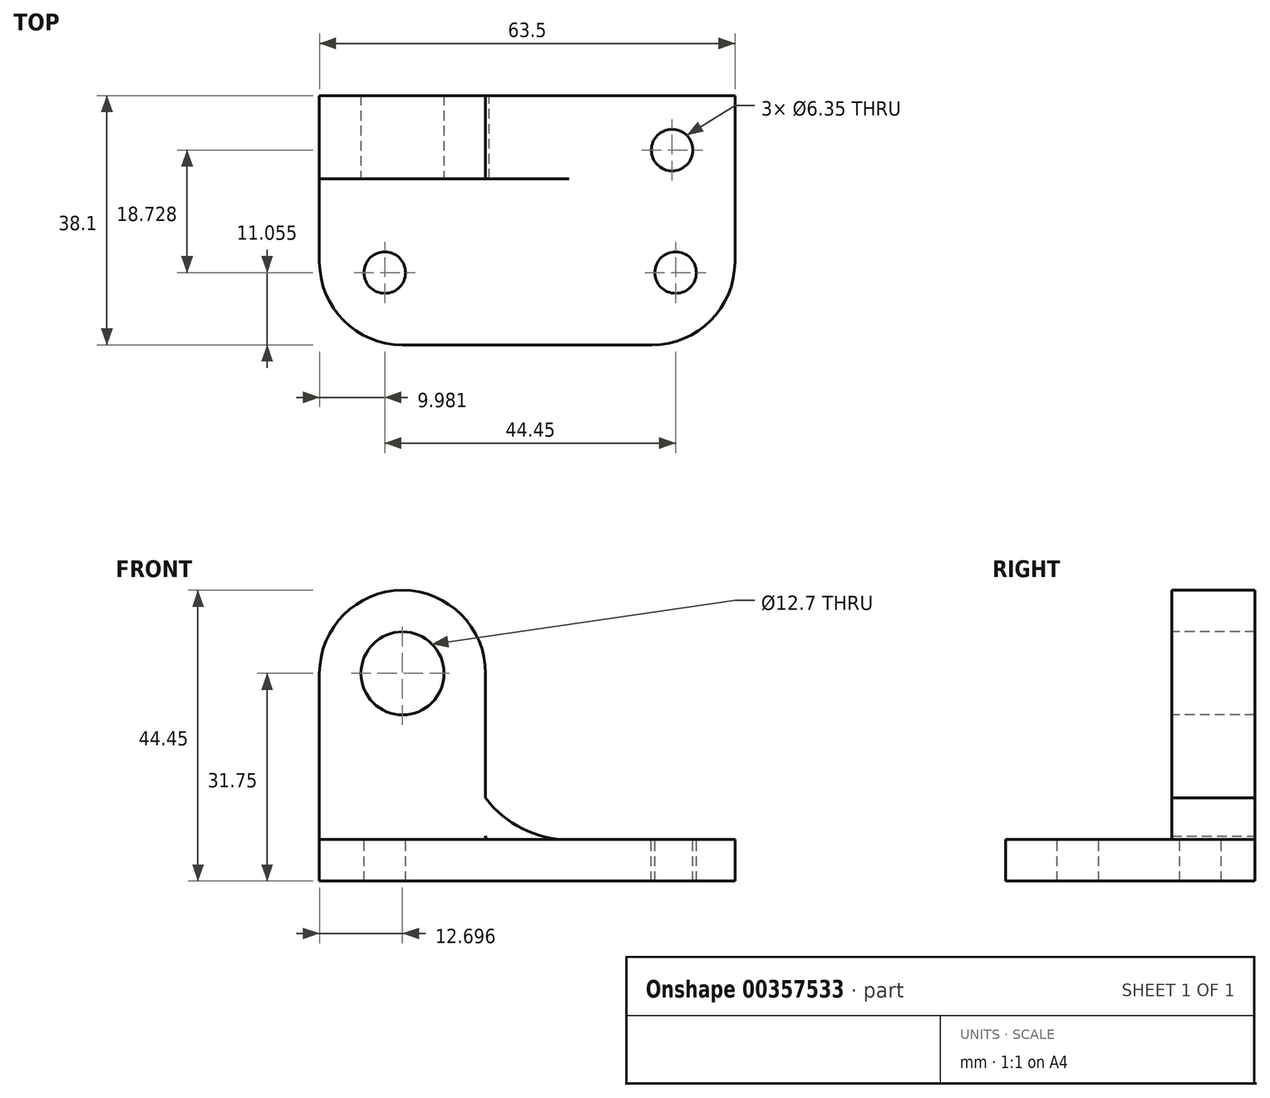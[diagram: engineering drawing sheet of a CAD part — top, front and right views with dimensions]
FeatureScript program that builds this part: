
annotation { "Feature Type Name" : "Feature", "Feature Type Description" : "" }
export const myFeature = defineFeature(function(context is Context, id is Id, definition is map)
    precondition{}
    {
        {
            var Q0;
            Q0=qCreatedBy(makeId("Front.planeOp"),FACE);
            var sketch = newSketch(context, id + "F0", { "sketchPlane" : qUnion([Q0])});
            skLineSegment(sketch, "E0", {"start": v(-62.41, 45.13) * mm, "end": v(-37.01, 45.13) * mm});
            skLineSegment(sketch, "E1", {"start": v(-37.01, 45.13) * mm, "end": v(-37.01, 7.03) * mm});
            skLineSegment(sketch, "E2", {"start": v(-37.01, 7.03) * mm, "end": v(1.09, 7.03) * mm});
            skLineSegment(sketch, "E3", {"start": v(1.09, 7.03) * mm, "end": v(1.09, 0.68) * mm});
            skLineSegment(sketch, "E4", {"start": v(1.09, 0.68) * mm, "end": v(-62.41, 0.68) * mm});
            skLineSegment(sketch, "E5", {"start": v(-62.41, 0.68) * mm, "end": v(-62.41, 45.13) * mm});
            skSolve(sketch);
        }
        {
            var Q0;
            Q0=makeQuery(id+"F0.imprint","IMPRINT",FACE,{"disambiguationData":[TD([[makeQuery(id+"F0.imprint","IMPRINT",EDGE,{"derivedFrom":sQuery(id+"F0.wireOp",EDGE,"E0")}),-1.0]])]});
            extrude(context, id + "F1", {"entities" : qUnion([Q0]), "depth" : 38.1 * mm});
        }
        {
            var Q0;
            Q0=makeQuery(id+"F1.opExtrude","CAP_FACE",FACE,{"disambiguationData":[OSD([sQuery(id+"F0.wireOp",EDGE,"E0"),sQuery(id+"F0.wireOp",EDGE,"E1"),sQuery(id+"F0.wireOp",EDGE,"E2"),sQuery(id+"F0.wireOp",EDGE,"E3"),sQuery(id+"F0.wireOp",EDGE,"E4"),sQuery(id+"F0.wireOp",EDGE,"E5")])],"isStart":false});
            var sketch = newSketch(context, id + "F2", { "sketchPlane" : qUnion([Q0])});
            skLineSegment(sketch, "E6", {"start": v(-37.01, 7.03) * mm, "end": v(-62.41, 7.03) * mm});
            skSolve(sketch);
        }
        {
            var Q0;
            {var subQ0=sQuery(id+"F2.wireOp",EDGE,"E6");Q0=makeQuery(id+"F2.imprint","IMPRINT",FACE,{"disambiguationData":[TD([[makeQuery(id+"F2.imprint","IMPRINT",EDGE,{"derivedFrom":subQ0}),-1.0]])]});}
            extrude(context, id + "F3", {"entities" : qUnion([Q0]), "operationType" : NewBodyOperationType.REMOVE, "oppositeDirection" : true, "depth" : 25.4 * mm});
        }
        {
            var Q0;
            Q0=makeQuery(id+"F3.boolean.opBoolean","COPY",FACE,{"derivedFrom":makeQuery(id+"F3.opExtrude","CAP_FACE",FACE,{"disambiguationData":[OSD([sQuery(id+"F0.wireOp",EDGE,"E0"),sQuery(id+"F0.wireOp",EDGE,"E1"),sQuery(id+"F0.wireOp",EDGE,"E5"),sQuery(id+"F2.wireOp",EDGE,"E6")])],"isStart":false})});
            var sketch = newSketch(context, id + "F4", { "sketchPlane" : qUnion([Q0])});
            skLineSegment(sketch, "E7", {"start": v(-62.41, 7.03) * mm, "end": v(-62.41, 32.43) * mm});
            skLineSegment(sketch, "E8", {"start": v(-49.71, 45.13) * mm, "end": v(-49.71, 45.13) * mm});
            skLineSegment(sketch, "E9", {"start": v(-37.01, 32.43) * mm, "end": v(-37.01, 7.03) * mm});
            skPoint(sketch, "E10.visualSharp", {"position": v(-62.41, 45.13) * mm});
            skArc(sketch, "E10.filletArc", {"start": v(-49.71, 45.13) * mm, "mid": v(-58.7, 41.41) * mm, "end": v(-62.41, 32.43) * mm});
            skPoint(sketch, "E11.visualSharp", {"position": v(-37.01, 45.13) * mm});
            skArc(sketch, "E11.filletArc", {"start": v(-37.01, 32.43) * mm, "mid": v(-40.73, 41.41) * mm, "end": v(-49.71, 45.13) * mm});
            skCircle(sketch, "E12", {"center": v(-49.71, 32.43) * mm, "radius": 6.35 * mm});
            skSolve(sketch);
        }
        {
            var Q0;
            {var subQ0=sQuery(id+"F4.wireOp",EDGE,"E10.filletArc");Q0=makeQuery(id+"F4.imprint","IMPRINT",FACE,{"disambiguationData":[TD([[makeQuery(id+"F4.imprint","IMPRINT",EDGE,{"derivedFrom":subQ0}),-1.0]])]});}
            var Q1;
            {var subQ0=sQuery(id+"F4.wireOp",EDGE,"E11.filletArc");Q1=makeQuery(id+"F4.imprint","IMPRINT",FACE,{"disambiguationData":[TD([[makeQuery(id+"F4.imprint","IMPRINT",EDGE,{"derivedFrom":subQ0}),-1.0]])]});}
            var Q2;
            Q2=makeQuery(id+"F4.imprint","IMPRINT",FACE,{"disambiguationData":[TD([[makeQuery(id+"F4.imprint","IMPRINT",EDGE,{"derivedFrom":sQuery(id+"F4.wireOp",EDGE,"E12")}),1.0]])]});
            extrude(context, id + "F5", {"entities" : qUnion([Q0, Q1, Q2]), "operationType" : NewBodyOperationType.REMOVE, "oppositeDirection" : true, "depth" : 12.7 * mm});
        }
        {
            var Q0;
            Q0=makeQuery(id+"F3.boolean.opBoolean","MERGE",FACE,{"derivedFrom":[makeQuery(id+"F1.opExtrude","SWEPT_FACE",FACE,{"disambiguationData":[OSD([sQuery(id+"F0.wireOp",EDGE,"E2")])]}),makeQuery(id+"F3.opExtrude","SWEPT_FACE",FACE,{"disambiguationData":[OSD([sQuery(id+"F2.wireOp",EDGE,"E6")])]})]});
            var sketch = newSketch(context, id + "F6", { "sketchPlane" : qUnion([Q0])});
            skLineSegment(sketch, "E13", {"start": v(1.09, 0) * mm, "end": v(1.09, -25.4) * mm});
            skLineSegment(sketch, "E14", {"start": v(-11.61, -38.1) * mm, "end": v(-49.71, -38.1) * mm});
            skLineSegment(sketch, "E15", {"start": v(-62.41, -25.4) * mm, "end": v(-62.41, 0) * mm});
            skPoint(sketch, "E16.visualSharp", {"position": v(1.09, -38.1) * mm});
            skArc(sketch, "E16.filletArc", {"start": v(-11.61, -38.1) * mm, "mid": v(-2.63, -34.38) * mm, "end": v(1.09, -25.4) * mm});
            skPoint(sketch, "E17.visualSharp", {"position": v(-62.41, -38.1) * mm});
            skArc(sketch, "E17.filletArc", {"start": v(-62.41, -25.4) * mm, "mid": v(-58.7, -34.38) * mm, "end": v(-49.71, -38.1) * mm});
            skCircle(sketch, "E18", {"center": v(-8.51, -8.32) * mm, "radius": 3.18 * mm});
            skCircle(sketch, "E19", {"center": v(-7.98, -27.05) * mm, "radius": 3.18 * mm});
            skLineSegment(sketch, "E20", {"start": v(-7.98, -27.05) * mm, "end": v(-8.51, -8.32) * mm});
            skLineSegment(sketch, "E21", {"start": v(-7.98, -27.05) * mm, "end": v(-52.43, -27.05) * mm});
            skCircle(sketch, "E22", {"center": v(-52.43, -27.05) * mm, "radius": 3.18 * mm});
            skSolve(sketch);
        }
        {
            var Q0;
            {var subQ0=sQuery(id+"F6.wireOp",EDGE,"E16.filletArc");Q0=makeQuery(id+"F6.imprint","IMPRINT",FACE,{"disambiguationData":[TD([[makeQuery(id+"F6.imprint","IMPRINT",EDGE,{"derivedFrom":subQ0}),-1.0]])]});}
            var Q1;
            {var subQ0=sQuery(id+"F6.wireOp",EDGE,"E17.filletArc");Q1=makeQuery(id+"F6.imprint","IMPRINT",FACE,{"disambiguationData":[TD([[makeQuery(id+"F6.imprint","IMPRINT",EDGE,{"derivedFrom":subQ0}),-1.0]])]});}
            extrude(context, id + "F7", {"entities" : qUnion([Q0, Q1]), "operationType" : NewBodyOperationType.REMOVE, "oppositeDirection" : true, "depth" : 6.35 * mm});
        }
        {
            var Q0;
            Q0 = qSketchRegion(id + "F6", true);
            extrude(context, id + "F8", {"entities" : qUnion([Q0]), "operationType" : NewBodyOperationType.REMOVE, "oppositeDirection" : true, "depth" : 6.35 * mm});
        }
        {
            var Q0;
            Q0=makeQuery(id+"F1.opExtrude","CAP_FACE",FACE,{"disambiguationData":[OSD([sQuery(id+"F0.wireOp",EDGE,"E0"),sQuery(id+"F0.wireOp",EDGE,"E1"),sQuery(id+"F0.wireOp",EDGE,"E2"),sQuery(id+"F0.wireOp",EDGE,"E3"),sQuery(id+"F0.wireOp",EDGE,"E4"),sQuery(id+"F0.wireOp",EDGE,"E5")])],"isStart":true});
            var sketch = newSketch(context, id + "F9", { "sketchPlane" : qUnion([Q0])});
            skLineSegment(sketch, "E23", {"start": v(37.01, 13.38) * mm, "end": v(24.31, 13.38) * mm});
            skLineSegment(sketch, "E24", {"start": v(24.31, 13.38) * mm, "end": v(24.31, 7.03) * mm});
            skLineSegment(sketch, "E25", {"start": v(24.31, 7.03) * mm, "end": v(24.31, 7.03) * mm});
            skPoint(sketch, "E26.visualSharp", {"position": v(37.01, 7.03) * mm});
            skPoint(sketch, "E27.visualSharp", {"position": v(37.01, 19.73) * mm});
            skLineSegment(sketch, "E27.filletArc", {"start": v(37.01, 19.73) * mm, "end": v(37.01, 19.73) * mm});
            skLineSegment(sketch, "E28", {"start": v(37.01, 13.38) * mm, "end": v(37.01, 7.57) * mm});
            skLineSegment(sketch, "E29", {"start": v(24.31, 7.03) * mm, "end": v(36.48, 7.03) * mm});
            skArc(sketch, "E30.filletArc", {"start": v(36.48, 7.03) * mm, "mid": v(36.86, 7.19) * mm, "end": v(37.01, 7.57) * mm});
            skArc(sketch, "E31", {"start": v(24.31, 7.03) * mm, "mid": v(31.41, 8.7) * mm, "end": v(37.01, 13.38) * mm});
            skSolve(sketch);
        }
        {
            var Q0;
            Q0=makeQuery(id+"F9.imprint","IMPRINT",FACE,{"disambiguationData":[TD([[makeQuery(id+"F9.imprint","IMPRINT",EDGE,{"derivedFrom":sQuery(id+"F9.wireOp",EDGE,"E28")}),-1.0]])]});
            extrude(context, id + "F10", {"entities" : qUnion([Q0]), "operationType" : NewBodyOperationType.ADD, "oppositeDirection" : true, "depth" : 12.7 * mm});
        }
    });
